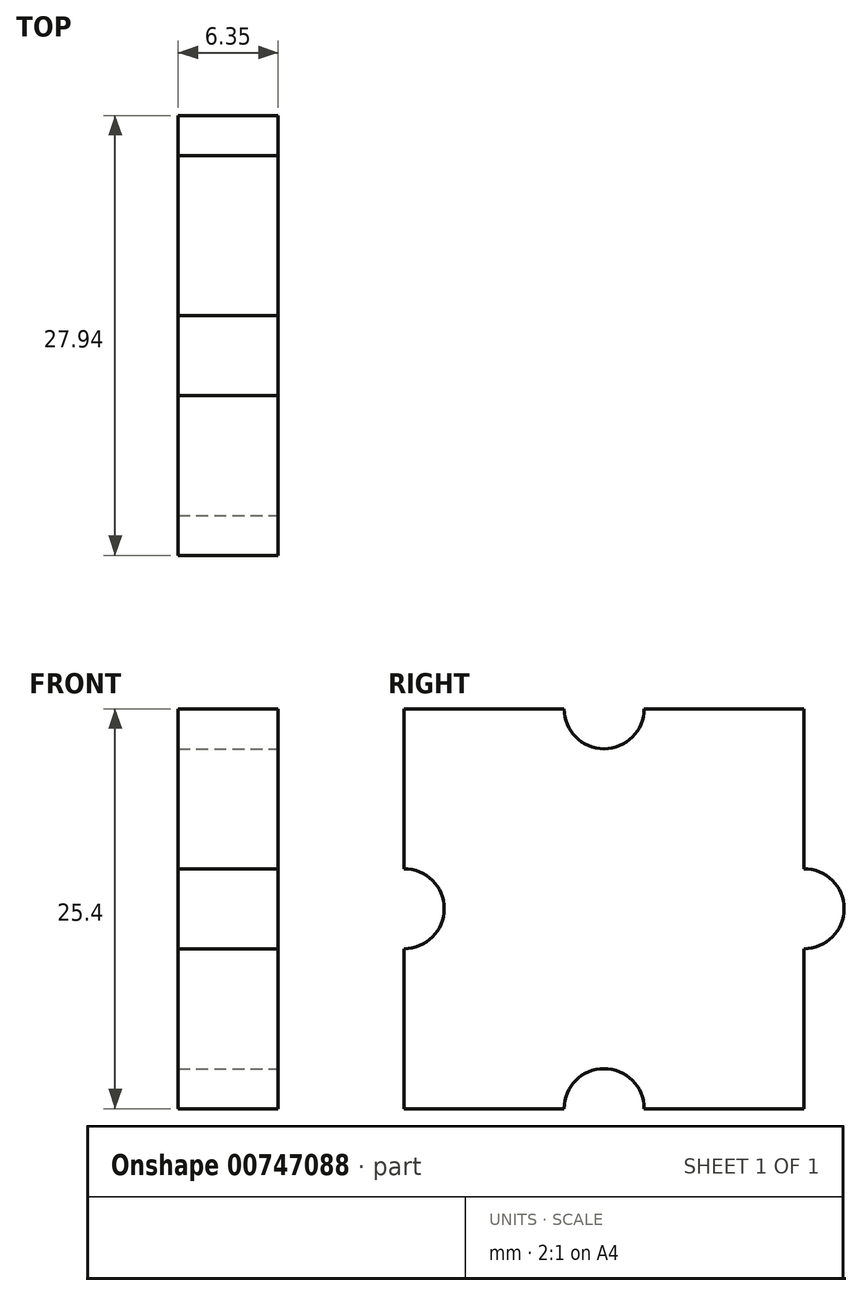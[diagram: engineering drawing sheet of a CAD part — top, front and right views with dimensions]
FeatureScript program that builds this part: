
annotation { "Feature Type Name" : "Feature", "Feature Type Description" : "" }
export const myFeature = defineFeature(function(context is Context, id is Id, definition is map)
    precondition{}
    {
        {
            var Q0;
            Q0=qCreatedBy(makeId("Right.planeOp"),FACE);
            var sketch = newSketch(context, id + "F0", { "sketchPlane" : qUnion([Q0])});
            skLineSegment(sketch, "E0", {"start": v(0, 0) * mm, "end": v(0, 25.4) * mm});
            skLineSegment(sketch, "E1", {"start": v(0, 25.4) * mm, "end": v(25.4, 25.4) * mm});
            skLineSegment(sketch, "E2", {"start": v(25.4, 25.4) * mm, "end": v(25.4, 0) * mm});
            skLineSegment(sketch, "E3", {"start": v(25.4, 0) * mm, "end": v(0, 0) * mm});
            skSolve(sketch);
        }
        {
            var Q0;
            Q0=qSketchRegion(id+"F0",true);
            extrude(context, id + "F1", {"entities" : qUnion([Q0]), "depth" : 6.35 * mm, "offsetDistance" : 25.4 * mm});
        }
        {
            var Q0;
            Q0=makeQuery(id+"F1.opExtrude","CAP_FACE",FACE,{"disambiguationData":[OSD([sQuery(id+"F0.wireOp",EDGE,"E0"),sQuery(id+"F0.wireOp",EDGE,"E1"),sQuery(id+"F0.wireOp",EDGE,"E2"),sQuery(id+"F0.wireOp",EDGE,"E3")])],"isStart":false});
            var sketch = newSketch(context, id + "F2", { "sketchPlane" : qUnion([Q0])});
            skCircle(sketch, "E4", {"center": v(12.7, 0) * mm, "radius": 2.54 * mm});
            skCircle(sketch, "E5", {"center": v(0, 12.7) * mm, "radius": 2.54 * mm});
            skCircle(sketch, "E6", {"center": v(12.7, 25.4) * mm, "radius": 2.54 * mm});
            skSolve(sketch);
        }
        {
            var Q0;
            Q0=qSketchRegion(id+"F2",true);
            extrude(context, id + "F3", {"entities" : qUnion([Q0]), "operationType" : NewBodyOperationType.REMOVE, "oppositeDirection" : true, "depth" : 6.35 * mm, "offsetDistance" : 25.4 * mm});
        }
        {
            var Q0;
            Q0=makeQuery(id+"F1.opExtrude","CAP_FACE",FACE,{"disambiguationData":[OSD([sQuery(id+"F0.wireOp",EDGE,"E0"),sQuery(id+"F0.wireOp",EDGE,"E1"),sQuery(id+"F0.wireOp",EDGE,"E2"),sQuery(id+"F0.wireOp",EDGE,"E3")])],"isStart":false});
            var sketch = newSketch(context, id + "F4", { "sketchPlane" : qUnion([Q0])});
            skCircle(sketch, "E7", {"center": v(25.4, 12.7) * mm, "radius": 2.54 * mm});
            skSolve(sketch);
        }
        {
            var Q0;
            Q0=qSketchRegion(id+"F4",true);
            extrude(context, id + "F5", {"entities" : qUnion([Q0]), "operationType" : NewBodyOperationType.ADD, "oppositeDirection" : true, "depth" : 6.35 * mm, "offsetDistance" : 25.4 * mm});
        }
    });
